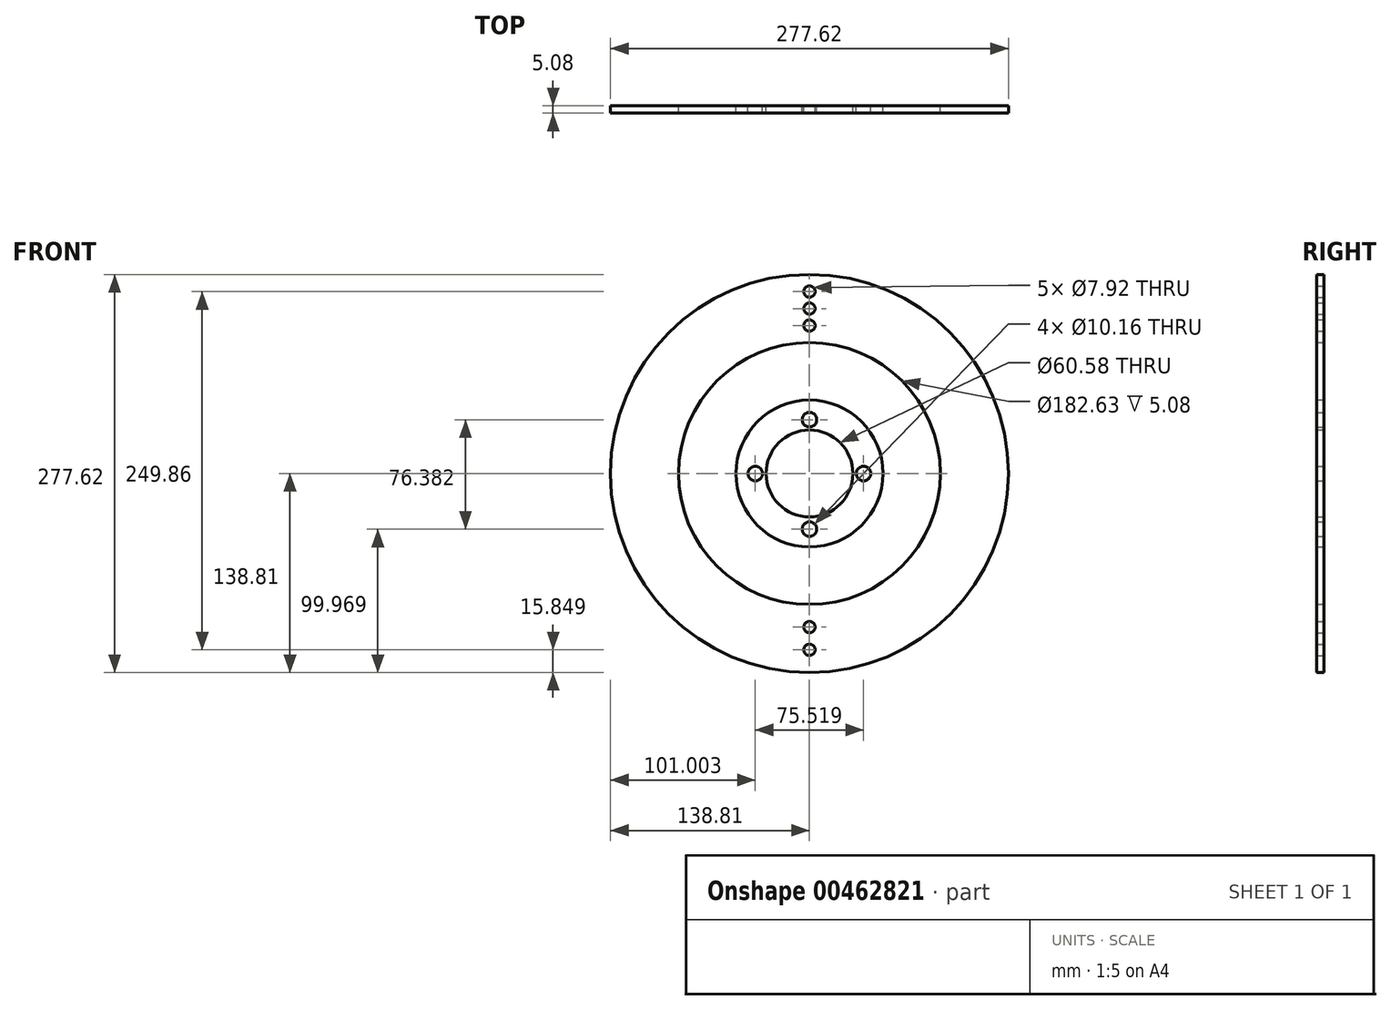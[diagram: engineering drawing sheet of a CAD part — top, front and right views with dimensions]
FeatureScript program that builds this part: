
annotation { "Feature Type Name" : "Feature", "Feature Type Description" : "" }
export const myFeature = defineFeature(function(context is Context, id is Id, definition is map)
    precondition{}
    {
        {
            var Q0;
            Q0=qCreatedBy(makeId("Front.planeOp"),FACE);
            var sketch = newSketch(context, id + "F0", { "sketchPlane" : qUnion([Q0])});
            skCircle(sketch, "E0", {"center": v(0, 0) * mm, "radius": 138.81 * mm});
            skCircle(sketch, "E1", {"center": v(0, 0) * mm, "radius": 91.31 * mm});
            skCircle(sketch, "E2", {"center": v(0, 0) * mm, "radius": 30.29 * mm});
            skCircle(sketch, "E3", {"center": v(0, 0) * mm, "radius": 51.24 * mm});
            skSolve(sketch);
        }
        {
            var Q0;
            Q0=makeQuery(id+"F0.imprint","IMPRINT",FACE,{"disambiguationData":[TD([[makeQuery(id+"F0.imprint","IMPRINT",EDGE,{"derivedFrom":sQuery(id+"F0.wireOp",EDGE,"E1")}),1.0]])]});
            var sketch = newSketch(context, id + "F1", { "sketchPlane" : qUnion([Q0])});
            skPoint(sketch, "E4", {"position": v(0, 37.54) * mm});
            skPoint(sketch, "E5", {"position": v(0, -38.84) * mm});
            skPoint(sketch, "E6", {"position": v(37.71, 0) * mm});
            skPoint(sketch, "E7", {"position": v(-37.8, 0) * mm});
            skSolve(sketch);
        }
        {
            var Q0;
            Q0=makeQuery(id+"F0.imprint","IMPRINT",FACE,{"disambiguationData":[TD([[makeQuery(id+"F0.imprint","IMPRINT",EDGE,{"derivedFrom":sQuery(id+"F0.wireOp",EDGE,"E0")}),1.0]])]});
            var sketch = newSketch(context, id + "F2", { "sketchPlane" : qUnion([Q0])});
            skPoint(sketch, "E8", {"position": v(0, 103.17) * mm});
            skPoint(sketch, "E9", {"position": v(0, 115.04) * mm});
            skPoint(sketch, "E10", {"position": v(0, 126.9) * mm});
            skCircle(sketch, "E11", {"center": v(0, 103.17) * mm, "radius": 3.96 * mm});
            skCircle(sketch, "E12", {"center": v(0, 115.04) * mm, "radius": 3.96 * mm});
            skCircle(sketch, "E13", {"center": v(0, 126.9) * mm, "radius": 3.96 * mm});
            skCircle(sketch, "E14", {"center": v(0, 0) * mm, "radius": 103.17 * mm, "construction": true});
            skCircle(sketch, "E15", {"center": v(0, 0) * mm, "radius": 115.04 * mm, "construction": true});
            skCircle(sketch, "E16", {"center": v(0, 0) * mm, "radius": 126.9 * mm, "construction": true});
            skSolve(sketch);
        }
        {
            var Q0;
            Q0=makeQuery(id+"F0.imprint","IMPRINT",FACE,{"disambiguationData":[TD([[makeQuery(id+"F0.imprint","IMPRINT",EDGE,{"derivedFrom":sQuery(id+"F0.wireOp",EDGE,"E0")}),1.0]])]});
            extrude(context, id + "F3", {"entities" : qUnion([Q0]), "depth" : 5.08 * mm});
        }
        {
            var Q0;
            Q0 = qSketchRegion(id + "F2", true);
            extrude(context, id + "F4", {"entities" : qUnion([Q0]), "operationType" : NewBodyOperationType.REMOVE, "endBound" : BoundingType.THROUGH_ALL, "depth" : 25.4 * mm});
        }
        {
            var Q0;
            Q0=makeQuery(id+"F0.imprint","IMPRINT",FACE,{"disambiguationData":[TD([[makeQuery(id+"F0.imprint","IMPRINT",EDGE,{"derivedFrom":sQuery(id+"F0.wireOp",EDGE,"E0")}),1.0]])]});
            var sketch = newSketch(context, id + "F5", { "sketchPlane" : qUnion([Q0])});
            skPoint(sketch, "E17", {"position": v(0, -107.14) * mm});
            skPoint(sketch, "E18", {"position": v(0, -122.96) * mm});
            skSolve(sketch);
        }
        {
            var Q0;
            Q0=sQuery(id+"F5.wireOp",VERTEX,"E17");
            var Q1;
            Q1=sQuery(id+"F5.wireOp",VERTEX,"E18");
            var Q2;
            Q2=makeQuery(id+"F3.opExtrude","SWEPT_BODY",BODY,{"disambiguationData":[OSD([sQuery(id+"F0.wireOp",EDGE,"E0"),sQuery(id+"F0.wireOp",EDGE,"E1")])]});
            hole(context, id + "F6", {"style" : HoleStyle.SIMPLE, "endStyle" : HoleEndStyle.THROUGH, "oppositeDirection" : true, "holeDiameter" : 7.92 * mm, "isTappedThrough" : true, "tappedDepth" : 12.7 * mm, "tapClearance" : 3, "locations" : qUnion([Q0, Q1]), "scope" : qUnion([Q2])});
        }
        {
            var Q0;
            Q0=makeQuery(id+"F0.imprint","IMPRINT",FACE,{"disambiguationData":[TD([[makeQuery(id+"F0.imprint","IMPRINT",EDGE,{"derivedFrom":sQuery(id+"F0.wireOp",EDGE,"E2")}),-1.0]])]});
            extrude(context, id + "F7", {"entities" : qUnion([Q0]), "depth" : 5.08 * mm});
        }
        {
            var Q0;
            Q0=sQuery(id+"F1.wireOp",VERTEX,"E4");
            var Q1;
            Q1=sQuery(id+"F1.wireOp",VERTEX,"E6");
            var Q2;
            Q2=sQuery(id+"F1.wireOp",VERTEX,"E5");
            var Q3;
            Q3=sQuery(id+"F1.wireOp",VERTEX,"E7");
            var Q4;
            Q4=makeQuery(id+"F7.opExtrude","SWEPT_BODY",BODY,{"disambiguationData":[OSD([sQuery(id+"F0.wireOp",EDGE,"E2"),sQuery(id+"F0.wireOp",EDGE,"E3")])]});
            hole(context, id + "F8", {"style" : HoleStyle.SIMPLE, "endStyle" : HoleEndStyle.THROUGH, "oppositeDirection" : true, "holeDiameter" : 10.16 * mm, "isTappedThrough" : true, "tappedDepth" : 12.7 * mm, "tapClearance" : 3, "locations" : qUnion([Q0, Q1, Q2, Q3]), "scope" : qUnion([Q4])});
        }
    });
